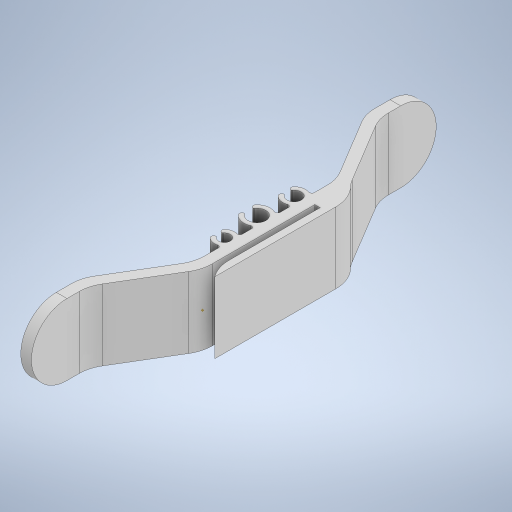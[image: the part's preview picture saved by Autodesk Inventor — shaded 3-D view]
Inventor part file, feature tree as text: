
AUTODESK INVENTOR PART (.ipt)
format: ipt  version: 2023 (Build 270158030, 158C)  size: 374,784 bytes
history: native  units: mm
features: fillet x4, extrude x2, sketch x2, other x1
ambient origin geometry x8: Origin, YZ Plane, XZ Plane, XY Plane, X Axis, Y Axis, Z Axis, Center Point
bodies: Body1 (feature_tree)
feature tree (9):
  extrude  "Extrusion2"  Depth=3.0mm
  fillet  "Fillet1"  Radius=3.0mm
  fillet  "Fillet2"  Radius=17.0mm
  extrude  "Extrusion3"  Depth=12.0mm
  fillet  "Fillet3"  Radius=20.0mm
  fillet  "Fillet4"  Radius=114.0mm
  sketch  "Sketch2"  dims[d9=3.0mm d16=3.0mm d17=3.0mm d18=17.0mm]
  other  "cable holder"
  sketch  "Sketch4"  dims[d19=20.0mm d20=12.0mm d21=20.0mm d22=114.0mm d23=20.0mm d24=20.0mm d25=17.0mm d28=20.0mm d29=0.0mm d30=2.0mm d31=1.5mm d32=10.0mm d33=10.0mm d34=10.0mm d36=10.0mm d37=10.0mm d38=7.210321mm d39=7.25mm d40=3.3mm d41=4.0mm d42=5.0mm d43=1.2mm d44=1.2mm d45=1.2mm d46=2.5mm d47=1.25mm d48=1.65mm d49=0.825mm d50=2.0mm d51=1.0mm d52=20.0mm d53=0.0mm d54=0.7mm d55=0.7mm]
